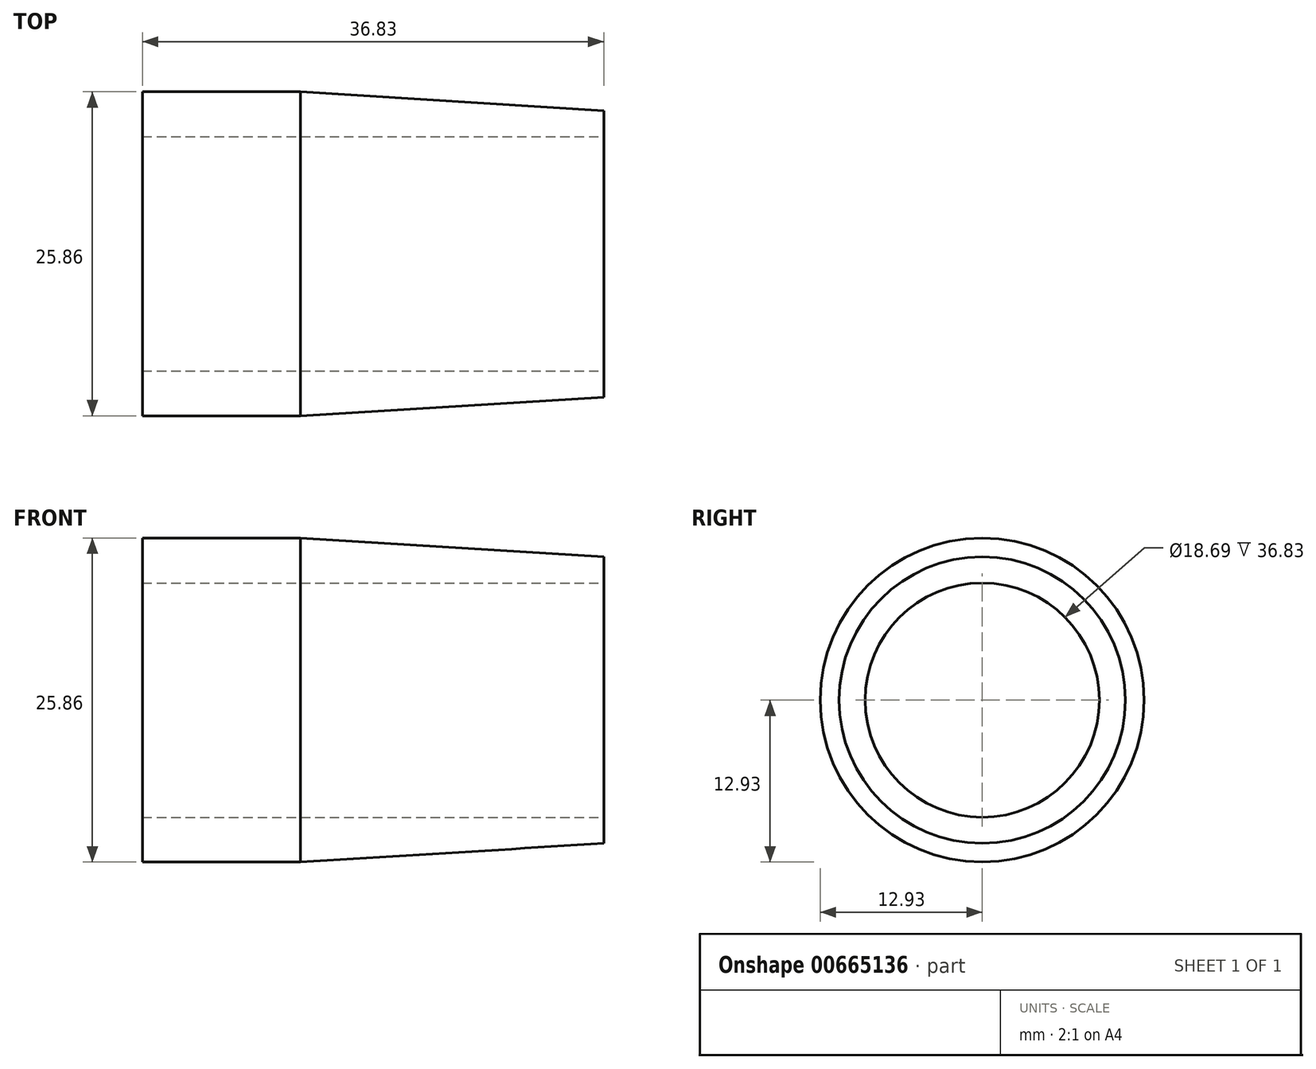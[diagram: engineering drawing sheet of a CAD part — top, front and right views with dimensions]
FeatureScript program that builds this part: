
annotation { "Feature Type Name" : "Feature", "Feature Type Description" : "" }
export const myFeature = defineFeature(function(context is Context, id is Id, definition is map)
    precondition{}
    {
        {
            var Q0;
            Q0=qCreatedBy(makeId("Right.planeOp"),FACE);
            var sketch = newSketch(context, id + "F0", { "sketchPlane" : qUnion([Q0])});
            skCircle(sketch, "E0", {"center": v(0, 0) * mm, "radius": 11.43 * mm});
            skSolve(sketch);
        }
        {
            var Q0;
            Q0=qCreatedBy(makeId("Right.planeOp"),FACE);
            cPlane(context, id + "F1", {"entities" : qUnion([Q0]), "cplaneType" : CPlaneType.OFFSET, "offset" : 24.2 * mm, "oppositeDirection" : true, "width" : 152.4 * mm, "height" : 152.4 * mm});
        }
        {
            var Q0;
            Q0=qCreatedBy(id+"F1.planeOp",FACE);
            var sketch = newSketch(context, id + "F2", { "sketchPlane" : qUnion([Q0])});
            skCircle(sketch, "E1", {"center": v(0, 0) * mm, "radius": 12.93 * mm});
            skSolve(sketch);
        }
        {
            var Q0;
            Q0 = qSketchRegion(id + "F2", true);
            extrude(context, id + "F3", {"entities" : qUnion([Q0]), "oppositeDirection" : true, "depth" : 12.62 * mm, "offsetDistance" : 25.4 * mm});
        }
        {
            var Q1;
            Q1=makeQuery(id+"F3.opExtrude","CAP_FACE",FACE,{"disambiguationData":[OSD([sQuery(id+"F2.wireOp",EDGE,"E1")])],"isStart":true});
            var Q2;
            Q2=makeQuery(id+"F0.imprint","IMPRINT",FACE,{"disambiguationData":[TD([[makeQuery(id+"F0.imprint","IMPRINT",EDGE,{"derivedFrom":sQuery(id+"F0.wireOp",EDGE,"E0")}),1.0]])]});
            loft(context, id + "F4", {"operationType" : NewBodyOperationType.ADD, "sheetProfilesArray" : [{ "sheetProfileEntities" : qUnion([Q1]) }, { "sheetProfileEntities" : qUnion([Q2]) }]});
        }
        {
            var Q0;
            Q0=makeQuery(id+"F4.opLoft","CAP_FACE",FACE,{"disambiguationData":[OSD([makeQuery(id+"F0.imprint","IMPRINT",FACE,{"disambiguationData":[TD([[makeQuery(id+"F0.imprint","IMPRINT",EDGE,{"derivedFrom":sQuery(id+"F0.wireOp",EDGE,"E0")}),1.0]])]})])],"isStart":true});
            var sketch = newSketch(context, id + "F5", { "sketchPlane" : qUnion([Q0])});
            skCircle(sketch, "E2", {"center": v(0, 0) * mm, "radius": 9.35 * mm});
            skSolve(sketch);
        }
        {
            var Q0;
            Q0 = qSketchRegion(id + "F5", true);
            extrude(context, id + "F6", {"entities" : qUnion([Q0]), "operationType" : NewBodyOperationType.REMOVE, "endBound" : BoundingType.THROUGH_ALL, "oppositeDirection" : true, "depth" : 25.4 * mm, "offsetDistance" : 25.4 * mm});
        }
    });
